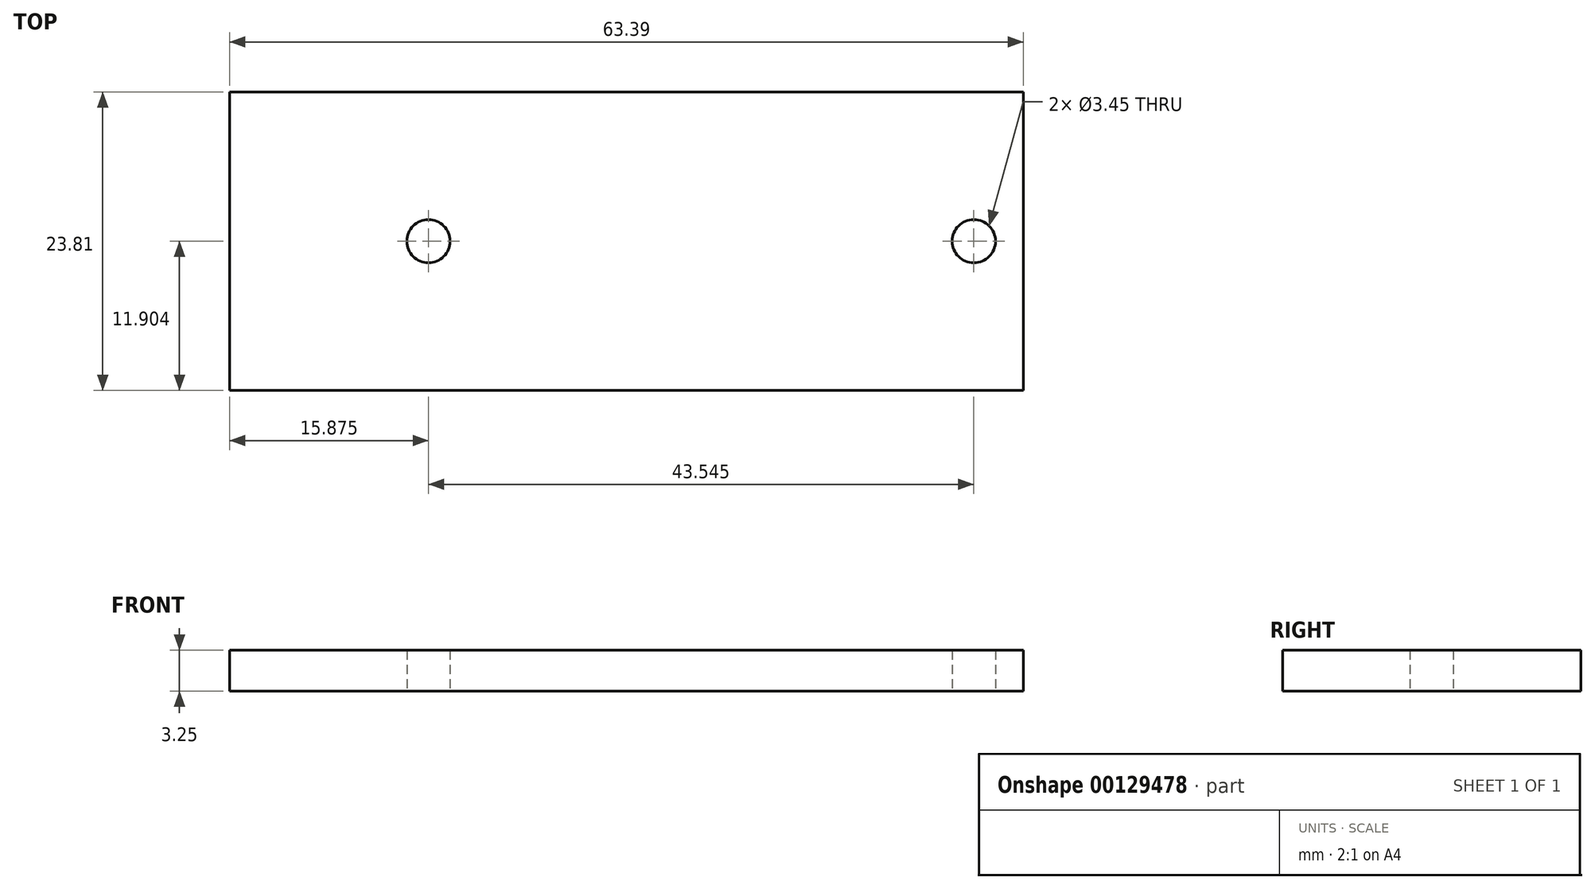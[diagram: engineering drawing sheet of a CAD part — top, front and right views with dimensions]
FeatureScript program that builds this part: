
annotation { "Feature Type Name" : "Feature", "Feature Type Description" : "" }
export const myFeature = defineFeature(function(context is Context, id is Id, definition is map)
    precondition{}
    {
        {
            var Q0;
            Q0=qCreatedBy(makeId("Top.planeOp"),FACE);
            var sketch = newSketch(context, id + "F0", { "sketchPlane" : qUnion([Q0])});
            skLineSegment(sketch, "E0.bottom", {"start": v(0, 0) * mm, "end": v(63.39, 0) * mm});
            skLineSegment(sketch, "E0.top", {"start": v(0, -23.81) * mm, "end": v(63.39, -23.81) * mm});
            skLineSegment(sketch, "E0.left", {"start": v(0, 0) * mm, "end": v(0, -23.81) * mm});
            skLineSegment(sketch, "E0.right", {"start": v(63.39, 0) * mm, "end": v(63.39, -23.81) * mm});
            skLineSegment(sketch, "E1", {"start": v(63.39, -11.9) * mm, "end": v(59.42, -11.9) * mm});
            skLineSegment(sketch, "E2", {"start": v(0, -11.9) * mm, "end": v(15.88, -11.9) * mm});
            skCircle(sketch, "E3", {"center": v(15.88, -11.9) * mm, "radius": 1.73 * mm});
            skCircle(sketch, "E4", {"center": v(59.42, -11.9) * mm, "radius": 1.73 * mm});
            skSolve(sketch);
        }
        {
            var Q0;
            Q0=qSketchRegion(id+"F0",true);
            extrude(context, id + "F1", {"entities" : qUnion([Q0]), "depth" : 3.25 * mm});
        }
    });
